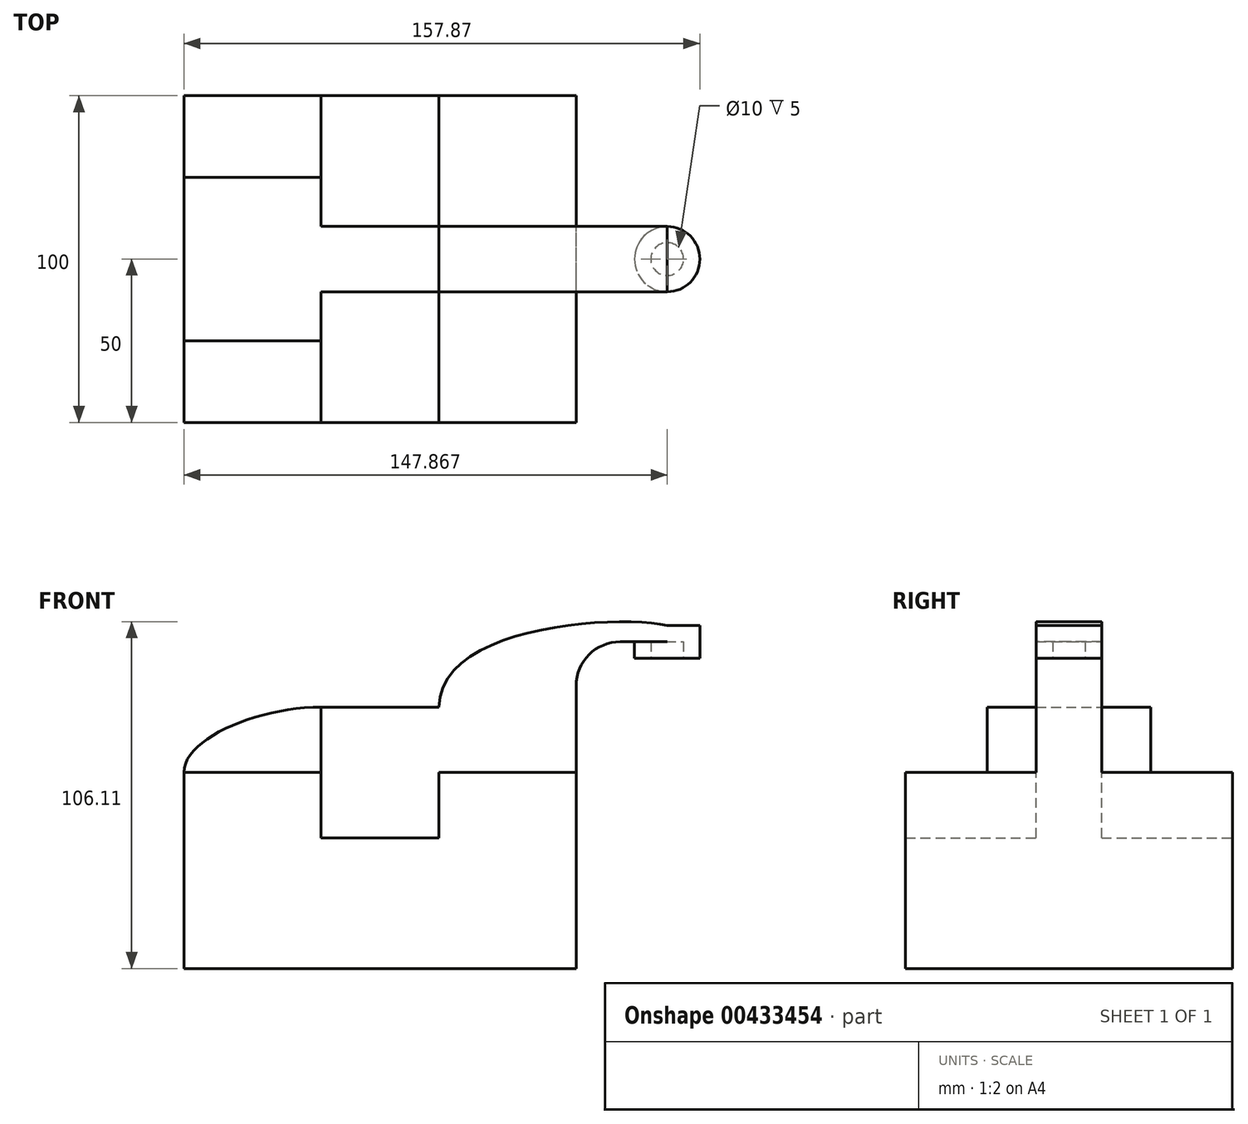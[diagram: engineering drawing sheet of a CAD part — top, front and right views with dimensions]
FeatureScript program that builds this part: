
annotation { "Feature Type Name" : "Feature", "Feature Type Description" : "" }
export const myFeature = defineFeature(function(context is Context, id is Id, definition is map)
    precondition{}
    {
        {
            var Q0;
            Q0=qCreatedBy(makeId("Front.planeOp"),FACE);
            var sketch = newSketch(context, id + "F0", { "sketchPlane" : qUnion([Q0])});
            skLineSegment(sketch, "E0.bottom", {"start": v(60, -30) * mm, "end": v(-60, -30) * mm});
            skLineSegment(sketch, "E0.top", {"start": v(60, 30) * mm, "end": v(-60, 30) * mm});
            skLineSegment(sketch, "E0.left", {"start": v(60, -30) * mm, "end": v(60, 30) * mm});
            skLineSegment(sketch, "E0.right", {"start": v(-60, -30) * mm, "end": v(-60, 30) * mm});
            skPoint(sketch, "E0.middle", {"position": v(0, 0) * mm});
            skLineSegment(sketch, "E1.bottom", {"start": v(97.87, 65) * mm, "end": v(87.87, 65) * mm});
            skLineSegment(sketch, "E1.top", {"start": v(97.87, 75) * mm, "end": v(87.87, 75) * mm});
            skLineSegment(sketch, "E1.left", {"start": v(97.87, 65) * mm, "end": v(97.87, 75) * mm});
            skLineSegment(sketch, "E1.right", {"start": v(87.87, 65) * mm, "end": v(87.87, 75) * mm});
            skPoint(sketch, "E1.middle", {"position": v(92.87, 70) * mm});
            skLineSegment(sketch, "E2", {"start": v(60, 30) * mm, "end": v(60, 56.5) * mm});
            skArc(sketch, "E3", {"start": v(60, 56.5) * mm, "mid": v(63.95, 66.05) * mm, "end": v(73.5, 70) * mm});
            skLineSegment(sketch, "E4", {"start": v(73.5, 70) * mm, "end": v(92.87, 70) * mm});
            skLineSegment(sketch, "E5.bottom", {"start": v(18, 10) * mm, "end": v(-18, 10) * mm});
            skLineSegment(sketch, "E5.top", {"start": v(18, 50) * mm, "end": v(-18, 50) * mm});
            skLineSegment(sketch, "E5.left", {"start": v(18, 10) * mm, "end": v(18, 50) * mm});
            skLineSegment(sketch, "E5.right", {"start": v(-18, 10) * mm, "end": v(-18, 50) * mm});
            skPoint(sketch, "E5.middle", {"position": v(0, 30) * mm});
            skFitSpline(sketch, "E6", {"points": [v(-60, 30) * mm, v(-18, 50) * mm], "startDerivative": vector(0, 31.34) * mm, "endDerivative": vector(57.65, 0) * mm});
            skFitSpline(sketch, "E7", {"points": [v(18, 50) * mm, v(87.87, 75) * mm], "startDerivative": vector(0.92, 75.46) * mm, "endDerivative": vector(46.01, -10.12) * mm});
            skFitSpline(sketch, "E8", {"points": [v(60, 30) * mm, v(87.87, 65) * mm], "startDerivative": vector(35.83, -5.45) * mm, "endDerivative": vector(9.2, 31.34) * mm});
            skLineSegment(sketch, "E9", {"start": v(92.87, 70) * mm, "end": v(92.87, 45) * mm});
            skLineSegment(sketch, "E10", {"start": v(92.87, 45) * mm, "end": v(78.6, 45) * mm});
            skSolve(sketch);
        }
        {
            var Q0;
            Q0=makeQuery(id+"F0.imprint","IMPRINT",FACE,{"disambiguationData":[TD([[makeQuery(id+"F0.imprint","IMPRINT",EDGE,{"derivedFrom":sQuery(id+"F0.wireOp",EDGE,"E0.bottom")}),-1.0]])]});
            extrude(context, id + "F1", {"entities" : qUnion([Q0]), "depth" : 100 * mm, "symmetric" : true});
        }
        {
            var Q0;
            {var subQ0=sQuery(id+"F0.wireOp",EDGE,"E6");Q0=makeQuery(id+"F0.imprint","IMPRINT",FACE,{"disambiguationData":[TD([[makeQuery(id+"F0.imprint","IMPRINT",EDGE,{"derivedFrom":subQ0}),-1.0]])]});}
            extrude(context, id + "F2", {"entities" : qUnion([Q0]), "operationType" : NewBodyOperationType.ADD, "depth" : 50 * mm, "symmetric" : true});
        }
        {
            var Q0;
            {var subQ5=sQuery(id+"F0.wireOp",EDGE,"E5.bottom");Q0=makeQuery(id+"F0.imprint","IMPRINT",FACE,{"disambiguationData":[TD([[makeQuery(id+"F0.imprint","IMPRINT",EDGE,{"derivedFrom":subQ5}),-1.0]])]});}
            extrude(context, id + "F3", {"entities" : qUnion([Q0]), "operationType" : NewBodyOperationType.ADD, "depth" : 20 * mm, "symmetric" : true});
        }
        {
            var Q0;
            {var subQ5=sQuery(id+"F0.wireOp",EDGE,"E5.top");Q0=makeQuery(id+"F0.imprint","IMPRINT",FACE,{"disambiguationData":[TD([[makeQuery(id+"F0.imprint","IMPRINT",EDGE,{"derivedFrom":subQ5}),1.0]])]});}
            var Q1;
            {var subQ1=sQuery(id+"F0.wireOp",EDGE,"E2");Q1=makeQuery(id+"F0.imprint","IMPRINT",FACE,{"disambiguationData":[TD([[makeQuery(id+"F0.imprint","IMPRINT",EDGE,{"derivedFrom":subQ1}),1.0]])]});}
            extrude(context, id + "F4", {"entities" : qUnion([Q0, Q1]), "operationType" : NewBodyOperationType.ADD, "depth" : 20 * mm, "symmetric" : true});
        }
        {
            var Q0;
            {var subQ1=sQuery(id+"F0.wireOp",EDGE,"E1.top");Q0=makeQuery(id+"F0.imprint","IMPRINT",FACE,{"disambiguationData":[TD([[makeQuery(id+"F0.imprint","IMPRINT",EDGE,{"derivedFrom":subQ1}),1.0]])]});}
            var Q1;
            Q1=sQuery(id+"F0.wireOp",EDGE,"E1.right");
            revolve(context, id + "F5", {"operationType" : NewBodyOperationType.ADD, "entities" : qUnion([Q0]), "axis" : qUnion([Q1]), "revolveType" : RevolveType.FULL});
        }
    });
